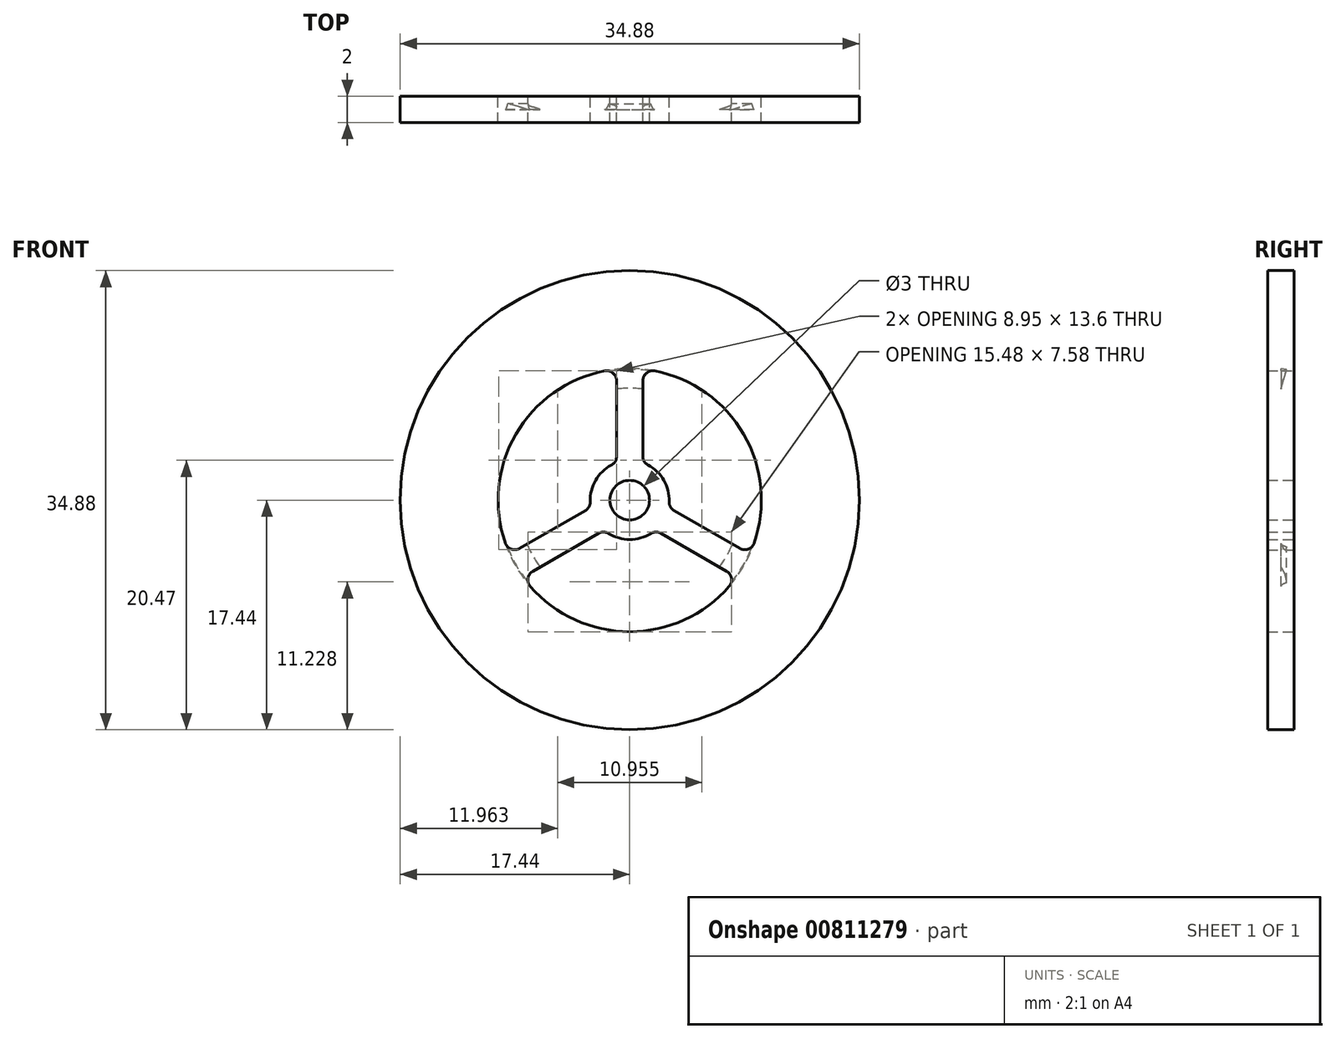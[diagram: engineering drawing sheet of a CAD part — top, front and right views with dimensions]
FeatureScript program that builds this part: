
annotation { "Feature Type Name" : "Feature", "Feature Type Description" : "" }
export const myFeature = defineFeature(function(context is Context, id is Id, definition is map)
    precondition{}
    {
        {
            var Q0;
            Q0=qCreatedBy(makeId("Front.planeOp"),FACE);
            var sketch = newSketch(context, id + "F0", { "sketchPlane" : qUnion([Q0])});
            skArc(sketch, "E0", {"start": v(-1.9, 9.82) * mm, "mid": v(-8.66, 5) * mm, "end": v(-9.45, -3.27) * mm});
            skCircle(sketch, "E1.0", {"center": v(0, 0) * mm, "radius": 17.44 * mm});
            skArc(sketch, "E2", {"start": v(-1.6, -2.54) * mm, "mid": v(0, -3) * mm, "end": v(1.6, -2.54) * mm});
            skCircle(sketch, "E3", {"center": v(0, 0) * mm, "radius": 1.5 * mm});
            skLineSegment(sketch, "E4.0", {"start": v(-1, 17.44) * mm, "end": v(-1, 17.41) * mm});
            skLineSegment(sketch, "E5.0", {"start": v(1, 17.44) * mm, "end": v(1, 17.41) * mm});
            skLineSegment(sketch, "E6.trimOffspring", {"start": v(-1, 9.08) * mm, "end": v(-1, 3.32) * mm});
            skLineSegment(sketch, "E7.trimOffspring", {"start": v(1, 9.08) * mm, "end": v(1, 3.32) * mm});
            skPoint(sketch, "E8.start.orphan", {"position": v(0, 17.44) * mm});
            skLineSegment(sketch, "E9.1.0", {"start": v(-7.36, -5.4) * mm, "end": v(-2.37, -2.53) * mm});
            skLineSegment(sketch, "E9.1.1", {"start": v(-8.36, -3.67) * mm, "end": v(-3.37, -0.8) * mm});
            skLineSegment(sketch, "E9.2.0", {"start": v(8.36, -3.67) * mm, "end": v(3.37, -0.8) * mm});
            skLineSegment(sketch, "E9.2.1", {"start": v(7.36, -5.4) * mm, "end": v(2.37, -2.53) * mm});
            skArc(sketch, "E10.trimOffspring", {"start": v(-7.56, -6.55) * mm, "mid": v(0, -10) * mm, "end": v(7.56, -6.55) * mm});
            skArc(sketch, "E11.trimOffspring", {"start": v(9.45, -3.27) * mm, "mid": v(8.66, 5) * mm, "end": v(1.9, 9.82) * mm});
            skArc(sketch, "E12.trimOffspring", {"start": v(3, -0.11) * mm, "mid": v(2.6, 1.5) * mm, "end": v(1.4, 2.65) * mm});
            skArc(sketch, "E13.trimOffspring", {"start": v(-1.4, 2.65) * mm, "mid": v(-2.6, 1.5) * mm, "end": v(-3, -0.11) * mm});
            skPoint(sketch, "E14.visualSharp", {"position": v(-1, 9.95) * mm});
            skArc(sketch, "E14.filletArc", {"start": v(-1, 9.08) * mm, "mid": v(-1.27, 9.66) * mm, "end": v(-1.9, 9.82) * mm});
            skPoint(sketch, "E15.visualSharp", {"position": v(-1, 2.83) * mm});
            skArc(sketch, "E15.filletArc", {"start": v(-1.4, 2.65) * mm, "mid": v(-1.1, 2.93) * mm, "end": v(-1, 3.32) * mm});
            skPoint(sketch, "E16.visualSharp", {"position": v(-2.95, -0.55) * mm});
            skArc(sketch, "E16.filletArc", {"start": v(-3.37, -0.8) * mm, "mid": v(-3.1, -0.5) * mm, "end": v(-3, -0.11) * mm});
            skPoint(sketch, "E17.visualSharp", {"position": v(-9.12, -4.1) * mm});
            skArc(sketch, "E17.filletArc", {"start": v(-9.45, -3.27) * mm, "mid": v(-9, -3.73) * mm, "end": v(-8.36, -3.67) * mm});
            skPoint(sketch, "E18.visualSharp", {"position": v(-8.12, -5.84) * mm});
            skArc(sketch, "E18.filletArc", {"start": v(-7.36, -5.4) * mm, "mid": v(-7.73, -5.93) * mm, "end": v(-7.56, -6.55) * mm});
            skPoint(sketch, "E19.visualSharp", {"position": v(-1.95, -2.28) * mm});
            skArc(sketch, "E19.filletArc", {"start": v(-1.6, -2.54) * mm, "mid": v(-1.98, -2.42) * mm, "end": v(-2.37, -2.53) * mm});
            skPoint(sketch, "E20.visualSharp", {"position": v(1.95, -2.28) * mm});
            skArc(sketch, "E20.filletArc", {"start": v(2.37, -2.53) * mm, "mid": v(1.98, -2.42) * mm, "end": v(1.6, -2.54) * mm});
            skPoint(sketch, "E21.visualSharp", {"position": v(8.12, -5.84) * mm});
            skArc(sketch, "E21.filletArc", {"start": v(7.56, -6.55) * mm, "mid": v(7.73, -5.93) * mm, "end": v(7.36, -5.4) * mm});
            skPoint(sketch, "E22.visualSharp", {"position": v(2.95, -0.55) * mm});
            skArc(sketch, "E22.filletArc", {"start": v(3, -0.11) * mm, "mid": v(3.1, -0.5) * mm, "end": v(3.37, -0.8) * mm});
            skPoint(sketch, "E23.visualSharp", {"position": v(1, 2.83) * mm});
            skArc(sketch, "E23.filletArc", {"start": v(1, 3.32) * mm, "mid": v(1.1, 2.93) * mm, "end": v(1.4, 2.65) * mm});
            skPoint(sketch, "E24.visualSharp", {"position": v(1, 9.95) * mm});
            skArc(sketch, "E24.filletArc", {"start": v(1.9, 9.82) * mm, "mid": v(1.27, 9.66) * mm, "end": v(1, 9.08) * mm});
            skPoint(sketch, "E25.visualSharp", {"position": v(9.12, -4.1) * mm});
            skArc(sketch, "E25.filletArc", {"start": v(8.36, -3.67) * mm, "mid": v(9, -3.73) * mm, "end": v(9.45, -3.27) * mm});
            skSolve(sketch);
        }
        {
            var Q0;
            Q0=makeQuery(id+"F0.imprint","IMPRINT",FACE,{"disambiguationData":[TD([[makeQuery(id+"F0.imprint","IMPRINT",EDGE,{"derivedFrom":sQuery(id+"F0.wireOp",EDGE,"E0")}),-1.0]])]});
            extrude(context, id + "F1", {"entities" : qUnion([Q0]), "endBound" : BoundingType.SYMMETRIC, "depth" : 2 * mm, "offsetDistance" : 25 * mm});
        }
        {
            var Q0;
            Q0=qCreatedBy(makeId("Right.planeOp"),FACE);
            var sketch = newSketch(context, id + "F2", { "sketchPlane" : qUnion([Q0])});
            skLineSegment(sketch, "E26", {"start": v(0, 10) * mm, "end": v(0, 8.5) * mm});
            skLineSegment(sketch, "E27", {"start": v(0, 8.5) * mm, "end": v(0.42, 9.94) * mm});
            skLineSegment(sketch, "E28", {"start": v(0.42, 9.94) * mm, "end": v(0, 10) * mm});
            skLineSegment(sketch, "E29", {"start": v(-23.04, 0) * mm, "end": v(18.64, 0) * mm, "construction": true});
            skLineSegment(sketch, "E30", {"start": v(18.64, 0) * mm, "end": v(23.06, 8.3) * mm, "construction": true});
            skSolve(sketch);
        }
        {
            var Q0;
            Q0 = qSketchRegion(id + "F2", true);
            var Q1;
            Q1=sQuery(id+"F2.wireOp",EDGE,"E29");
            revolve(context, id + "F3", {"operationType" : NewBodyOperationType.REMOVE, "surfaceOperationType" : NewSurfaceOperationType.NEW, "entities" : qUnion([Q0]), "axis" : qUnion([Q1]), "revolveType" : RevolveType.FULL, "oppositeDirection" : true});
        }
    });
